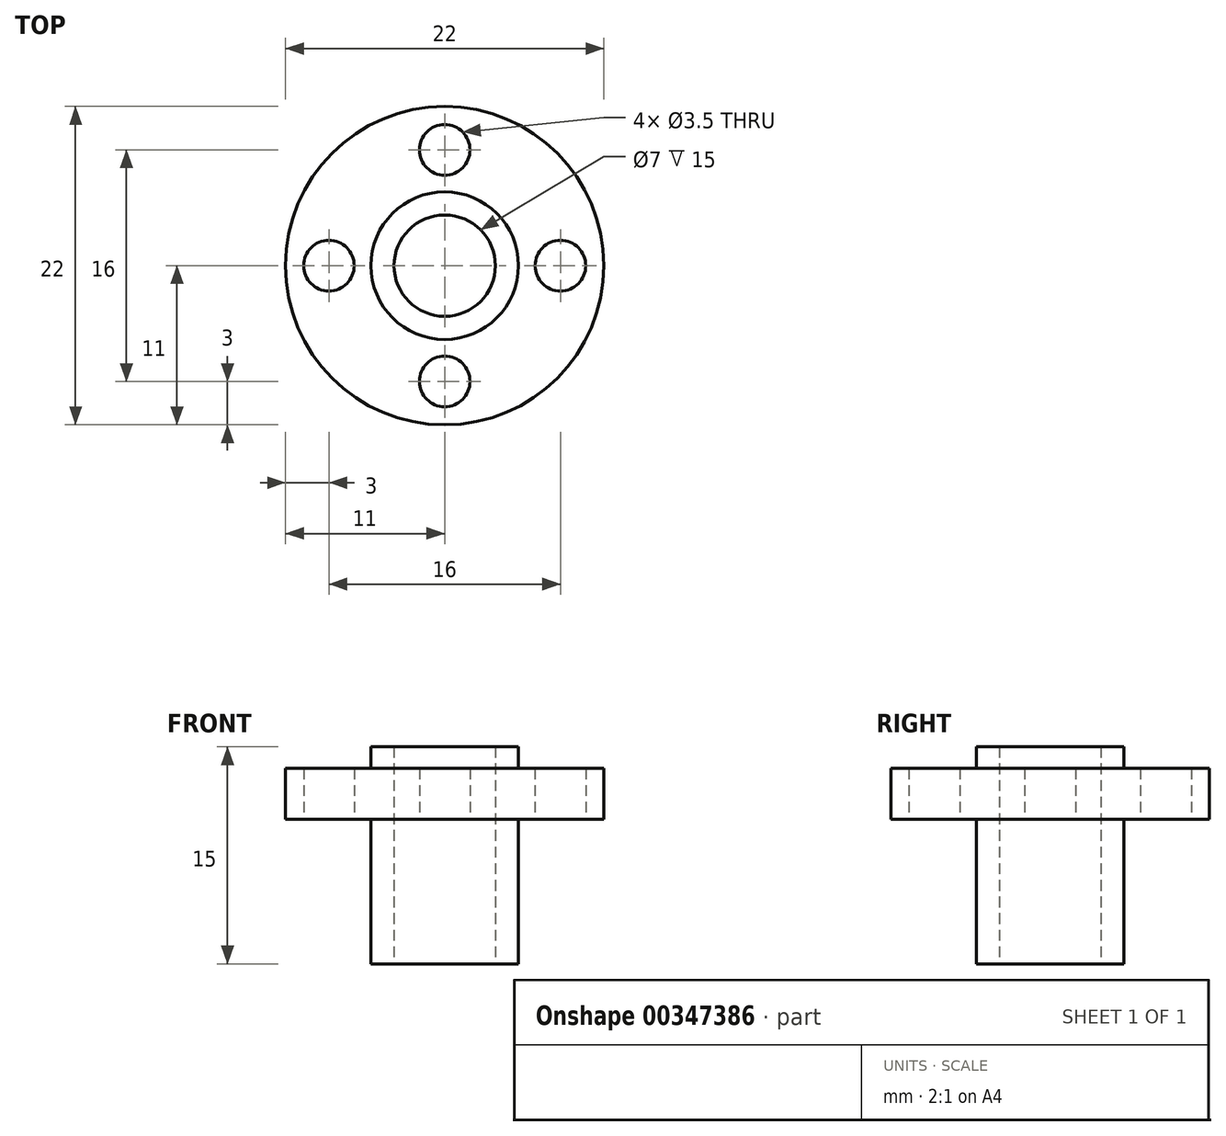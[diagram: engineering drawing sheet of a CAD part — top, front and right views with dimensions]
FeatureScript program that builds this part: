
annotation { "Feature Type Name" : "Feature", "Feature Type Description" : "" }
export const myFeature = defineFeature(function(context is Context, id is Id, definition is map)
    precondition{}
    {
        {
            var Q0;
            Q0=qCreatedBy(makeId("Top.planeOp"),FACE);
            var sketch = newSketch(context, id + "F0", { "sketchPlane" : qUnion([Q0])});
            skCircle(sketch, "E0", {"center": v(0, 0) * mm, "radius": 11 * mm});
            skCircle(sketch, "E1", {"center": v(0, 0) * mm, "radius": 8 * mm, "construction": true});
            skCircle(sketch, "E2", {"center": v(0, 0) * mm, "radius": 5.1 * mm});
            skCircle(sketch, "E3", {"center": v(0, 8) * mm, "radius": 1.75 * mm});
            skCircle(sketch, "E4.1.0", {"center": v(-8, 0) * mm, "radius": 1.75 * mm});
            skCircle(sketch, "E4.2.0", {"center": v(0, -8) * mm, "radius": 1.75 * mm});
            skCircle(sketch, "E4.3.0", {"center": v(8, 0) * mm, "radius": 1.75 * mm});
            skCircle(sketch, "E5", {"center": v(0, 0) * mm, "radius": 3.5 * mm});
            skSolve(sketch);
        }
        {
            var Q0;
            Q0 = qSketchRegion(id + "F0", true);
            extrude(context, id + "F1", {"entities" : qUnion([Q0]), "depth" : 3.5 * mm});
        }
        {
            var Q0;
            Q0=makeQuery(id+"F0.imprint","IMPRINT",FACE,{"disambiguationData":[TD([[makeQuery(id+"F0.imprint","IMPRINT",EDGE,{"derivedFrom":sQuery(id+"F0.wireOp",EDGE,"E2")}),1.0]])]});
            extrude(context, id + "F2", {"entities" : qUnion([Q0]), "operationType" : NewBodyOperationType.ADD, "depth" : (3.5 + 1.5) * mm});
        }
        {
            var Q0;
            Q0=makeQuery(id+"F0.imprint","IMPRINT",FACE,{"disambiguationData":[TD([[makeQuery(id+"F0.imprint","IMPRINT",EDGE,{"derivedFrom":sQuery(id+"F0.wireOp",EDGE,"E2")}),1.0]])]});
            extrude(context, id + "F3", {"entities" : qUnion([Q0]), "operationType" : NewBodyOperationType.ADD, "oppositeDirection" : true, "depth" : 10 * mm});
        }
    });
